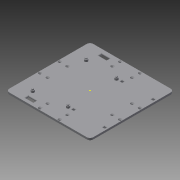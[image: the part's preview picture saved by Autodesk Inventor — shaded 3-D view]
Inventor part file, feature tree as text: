
AUTODESK INVENTOR PART (.ipt)
format: ipt  version: 2015 (Build 190159000, 159)  size: 353,792 bytes
history: native  units: in
note: dims shown in document units (in); Inventor stores cm internally (conversion verified against a paired STEP export)
features: sketch x13, extrude x10, fillet x7, mirror x6, plane x4, sweep x1, pattern_circular x1
ambient origin geometry x8: Origin, YZ Plane, XZ Plane, XY Plane, X Axis, Y Axis, Z Axis, Center Point
bodies: Solid1 (feature_tree)
feature tree (42):
  extrude  "Extrusion1"  Depth=2.5591in
  fillet  "Fillet1"  Radius=5.1181in
  extrude  "Extrusion6"  Depth=0.1181in TaperAngle=0.0deg
  extrude  "Extrusion7"  Depth=0.7205in
  plane  "Work Plane1"
  sweep  "Sweep1"
  plane  "Work Plane2"
  plane  "Work Plane3"
  mirror  "Mirror5"
  mirror  "Mirror6"
  mirror  "Mirror7"
  pattern_circular  "Circular Pattern3"  [2 undecoded]
  extrude  "Extrusion8"  TaperAngle=0.0deg  [1 undecoded]
  fillet  "Fillet2"  [1 undecoded]
  fillet  "Fillet3"  [1 undecoded]
  plane  "Work Plane4"
  mirror  "Mirror8"
  sketch  "Sketch15"  dims[d24=0.1181in]
  mirror  "Mirror9"
  extrude  "Extrusion9"  Depth=0.0197in TaperAngle=360.0deg
  fillet  "Fillet4"  Radius=2.1654in
  fillet  "Fillet5"  Radius=2.126in
  mirror  "Mirror10"
  extrude  "Extrusion10"  Depth=0.0197in
  extrude  "Extrusion11"  Depth=0.1181in
  extrude  "Extrusion12"  Depth=0.1181in
  extrude  "Extrusion13"  Depth=0.1181in TaperAngle=0.0deg
  extrude  "Extrusion14"  Depth=0.0394in
  fillet  "Fillet6"  Radius=0.0787in
  fillet  "Fillet7"  [1 undecoded]
  sketch  "Sketch1"  dims[d0=2.5591in d1=2.5591in d2=5.1181in]
  sketch  "Sketch6"  dims[d3=2.5591in d4=0.1181in d5=0.0in]
  sketch  "Sketch9"  dims[d16=0.1969in d20=0.7205in]
  sketch  "Sketch11"  dims[d21=0.7087in d22=0.7205in]
  sketch  "3D Sketch1"
  sketch  "Sketch14"  dims[d23=0.1181in]
  sketch  "Sketch16"  dims[d25=0.1181in]
  sketch  "Sketch17"  dims[d40=0.189in]
  sketch  "Sketch18"  dims[d41=0.189in]
  sketch  "Sketch19"  dims[d42=0.0591in d43=0.0in]
  sketch  "Sketch20"  dims[d44=0.0984in]
  sketch  "Sketch21"  dims[d45=0.0591in d46=0.0in d47=-0.6004in d48=0.0in d49=0.0in d51=-0.3543in d52=-2.5591in d53=1.5748in d54=360.0deg d56=2.1654in d57=2.126in d58=0.9055in d63=0.1181in d64=0.1181in d65=0.1181in d66=0.0in d67=0.0394in d68=0.0787in d69=-1.437in d70=2.0472in d71=2.0472in d72=2.126in d73=4.0157in d74=0.4724in d75=0.1969in d76=0.1181in d77=0.0in d78=0.0591in d79=0.0591in d80=0.315in d81=1.9984in d82=1.9984in d83=2.0984in d84=0.6in d85=0.1in d86=0.1969in d87=0.55in d88=0.1in d89=0.1969in d90=3.55in d91=0.1in d92=0.1969in d93=3.8in d94=0.1in d95=0.1969in d96=0.1181in d97=0.0in d98=0.1181in d99=0.0591in d100=0.0in d101=0.1181in d102=0.0591in d103=0.0in d104=0.1181in d105=0.0591in d106=0.0in d107=0.1181in d108=0.0591in d109=0.0in d110=0.0197in d111=0.0197in]
note: 6 required parameter values undecoded (feature->parameter linkage not recoverable at this tier; creation-order binding heuristic only, values carry confidence <= 0.55)
